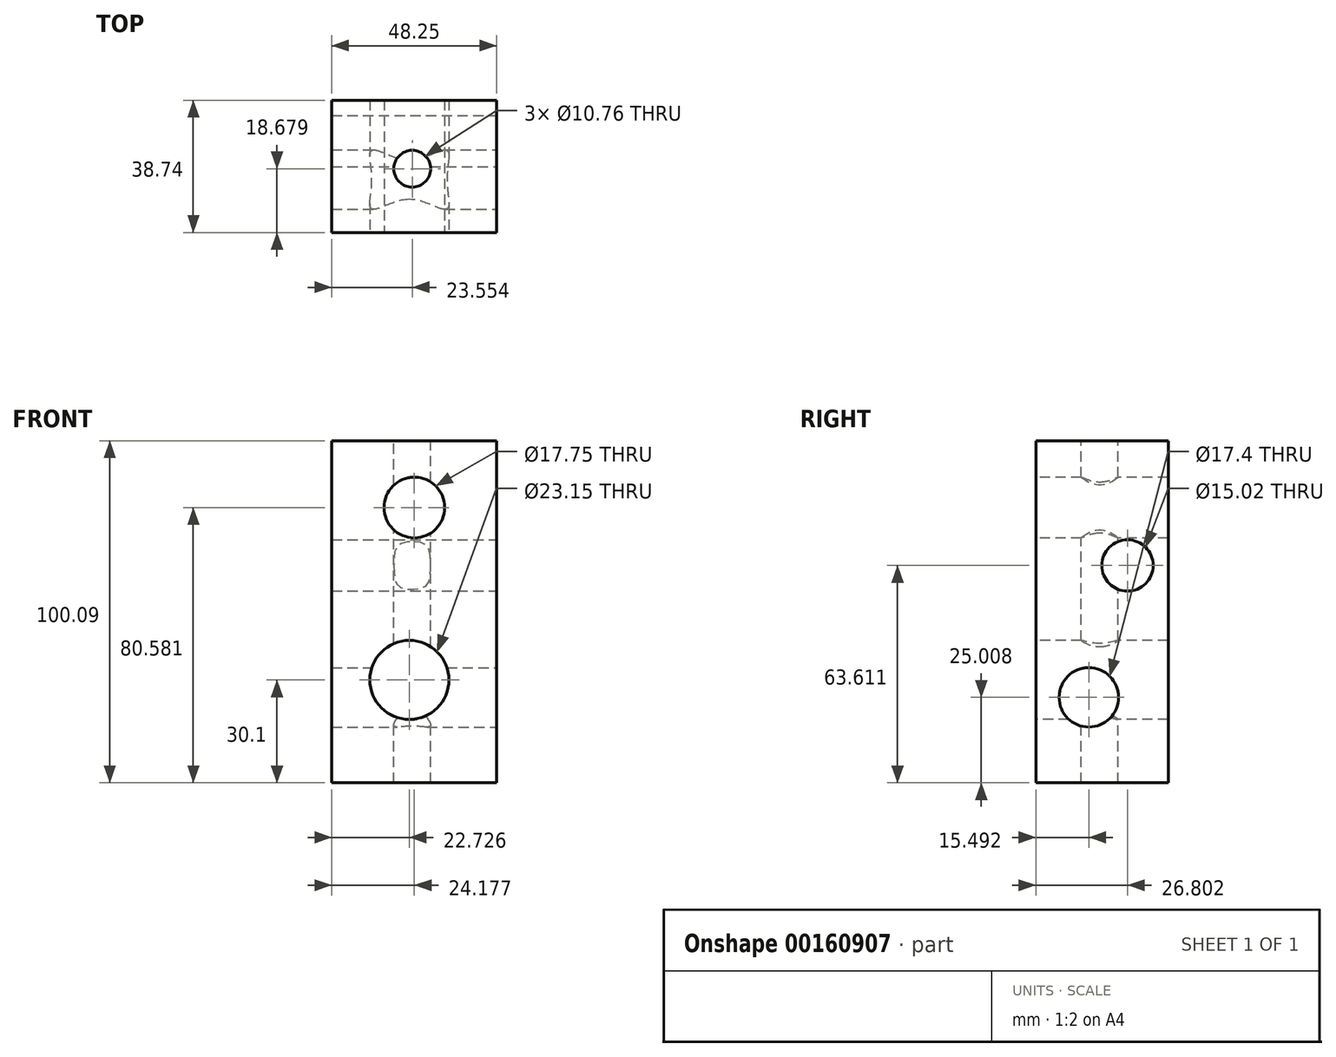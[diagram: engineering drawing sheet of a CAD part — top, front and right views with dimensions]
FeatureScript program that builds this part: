
annotation { "Feature Type Name" : "Feature", "Feature Type Description" : "" }
export const myFeature = defineFeature(function(context is Context, id is Id, definition is map)
    precondition{}
    {
        {
            var Q0;
            Q0=qCreatedBy(makeId("Front.planeOp"),FACE);
            var sketch = newSketch(context, id + "F0", { "sketchPlane" : qUnion([Q0])});
            skLineSegment(sketch, "E0.bottom", {"start": v(0, 0) * mm, "end": v(48.25, 0) * mm});
            skLineSegment(sketch, "E0.top", {"start": v(0, 100.09) * mm, "end": v(48.25, 100.09) * mm});
            skLineSegment(sketch, "E0.left", {"start": v(0, 0) * mm, "end": v(0, 100.09) * mm});
            skLineSegment(sketch, "E0.right", {"start": v(48.25, 0) * mm, "end": v(48.25, 100.09) * mm});
            skSolve(sketch);
        }
        {
            var Q0;
            Q0=makeQuery(id+"F0.imprint","IMPRINT",FACE,{"disambiguationData":[TD([[makeQuery(id+"F0.imprint","IMPRINT",EDGE,{"derivedFrom":sQuery(id+"F0.wireOp",EDGE,"E0.bottom")}),1.0]])]});
            extrude(context, id + "F1", {"entities" : qUnion([Q0]), "depth" : 38.73 * mm});
        }
        {
            var Q0;
            Q0=makeQuery(id+"F1.opExtrude","CAP_FACE",FACE,{"disambiguationData":[OSD([sQuery(id+"F0.wireOp",EDGE,"E0.bottom"),sQuery(id+"F0.wireOp",EDGE,"E0.top"),sQuery(id+"F0.wireOp",EDGE,"E0.left"),sQuery(id+"F0.wireOp",EDGE,"E0.right")])],"isStart":false});
            var sketch = newSketch(context, id + "F2", { "sketchPlane" : qUnion([Q0])});
            skCircle(sketch, "E1", {"center": v(24.18, 80.58) * mm, "radius": 8.88 * mm});
            skSolve(sketch);
        }
        {
            var Q0;
            Q0=makeQuery(id+"F2.imprint","IMPRINT",FACE,{"disambiguationData":[TD([[makeQuery(id+"F2.imprint","IMPRINT",EDGE,{"derivedFrom":sQuery(id+"F2.wireOp",EDGE,"E1")}),1.0]])]});
            extrude(context, id + "F3", {"entities" : qUnion([Q0]), "operationType" : NewBodyOperationType.REMOVE, "oppositeDirection" : true, "depth" : 72.39 * mm});
        }
        {
            var Q0;
            Q0=makeQuery(id+"F1.opExtrude","CAP_FACE",FACE,{"disambiguationData":[OSD([sQuery(id+"F0.wireOp",EDGE,"E0.bottom"),sQuery(id+"F0.wireOp",EDGE,"E0.top"),sQuery(id+"F0.wireOp",EDGE,"E0.left"),sQuery(id+"F0.wireOp",EDGE,"E0.right")])],"isStart":false});
            var sketch = newSketch(context, id + "F4", { "sketchPlane" : qUnion([Q0])});
            skCircle(sketch, "E2", {"center": v(22.73, 30.1) * mm, "radius": 11.58 * mm});
            skSolve(sketch);
        }
        {
            var Q0;
            Q0=makeQuery(id+"F4.imprint","IMPRINT",FACE,{"disambiguationData":[TD([[makeQuery(id+"F4.imprint","IMPRINT",EDGE,{"derivedFrom":sQuery(id+"F4.wireOp",EDGE,"E2")}),1.0]])]});
            extrude(context, id + "F5", {"entities" : qUnion([Q0]), "operationType" : NewBodyOperationType.REMOVE, "oppositeDirection" : true, "depth" : 81.9 * mm});
        }
        {
            var Q0;
            Q0=makeQuery(id+"F1.opExtrude","SWEPT_FACE",FACE,{"disambiguationData":[OSD([sQuery(id+"F0.wireOp",EDGE,"E0.right")])]});
            var sketch = newSketch(context, id + "F6", { "sketchPlane" : qUnion([Q0])});
            skCircle(sketch, "E3", {"center": v(-11.94, 63.61) * mm, "radius": 7.51 * mm});
            skCircle(sketch, "E4", {"center": v(-23.25, 25) * mm, "radius": 8.7 * mm});
            skSolve(sketch);
        }
        {
            var Q0;
            Q0=makeQuery(id+"F6.imprint","IMPRINT",FACE,{"disambiguationData":[TD([[makeQuery(id+"F6.imprint","IMPRINT",EDGE,{"derivedFrom":sQuery(id+"F6.wireOp",EDGE,"E3")}),1.0]])]});
            var Q1;
            Q1=makeQuery(id+"F6.imprint","IMPRINT",FACE,{"disambiguationData":[TD([[makeQuery(id+"F6.imprint","IMPRINT",EDGE,{"derivedFrom":sQuery(id+"F6.wireOp",EDGE,"E4")}),1.0]])]});
            extrude(context, id + "F7", {"entities" : qUnion([Q0, Q1]), "operationType" : NewBodyOperationType.REMOVE, "oppositeDirection" : true, "depth" : 74.3 * mm});
        }
        {
            var Q0;
            Q0=makeQuery(id+"F1.opExtrude","SWEPT_FACE",FACE,{"disambiguationData":[OSD([sQuery(id+"F0.wireOp",EDGE,"E0.top")])]});
            var sketch = newSketch(context, id + "F8", { "sketchPlane" : qUnion([Q0])});
            skCircle(sketch, "E5", {"center": v(23.55, -20.06) * mm, "radius": 5.38 * mm});
            skSolve(sketch);
        }
        {
            var Q0;
            Q0=makeQuery(id+"F8.imprint","IMPRINT",FACE,{"disambiguationData":[TD([[makeQuery(id+"F8.imprint","IMPRINT",EDGE,{"derivedFrom":sQuery(id+"F8.wireOp",EDGE,"E5")}),1.0]])]});
            extrude(context, id + "F9", {"entities" : qUnion([Q0]), "operationType" : NewBodyOperationType.REMOVE, "oppositeDirection" : true, "depth" : 137.8 * mm});
        }
    });
